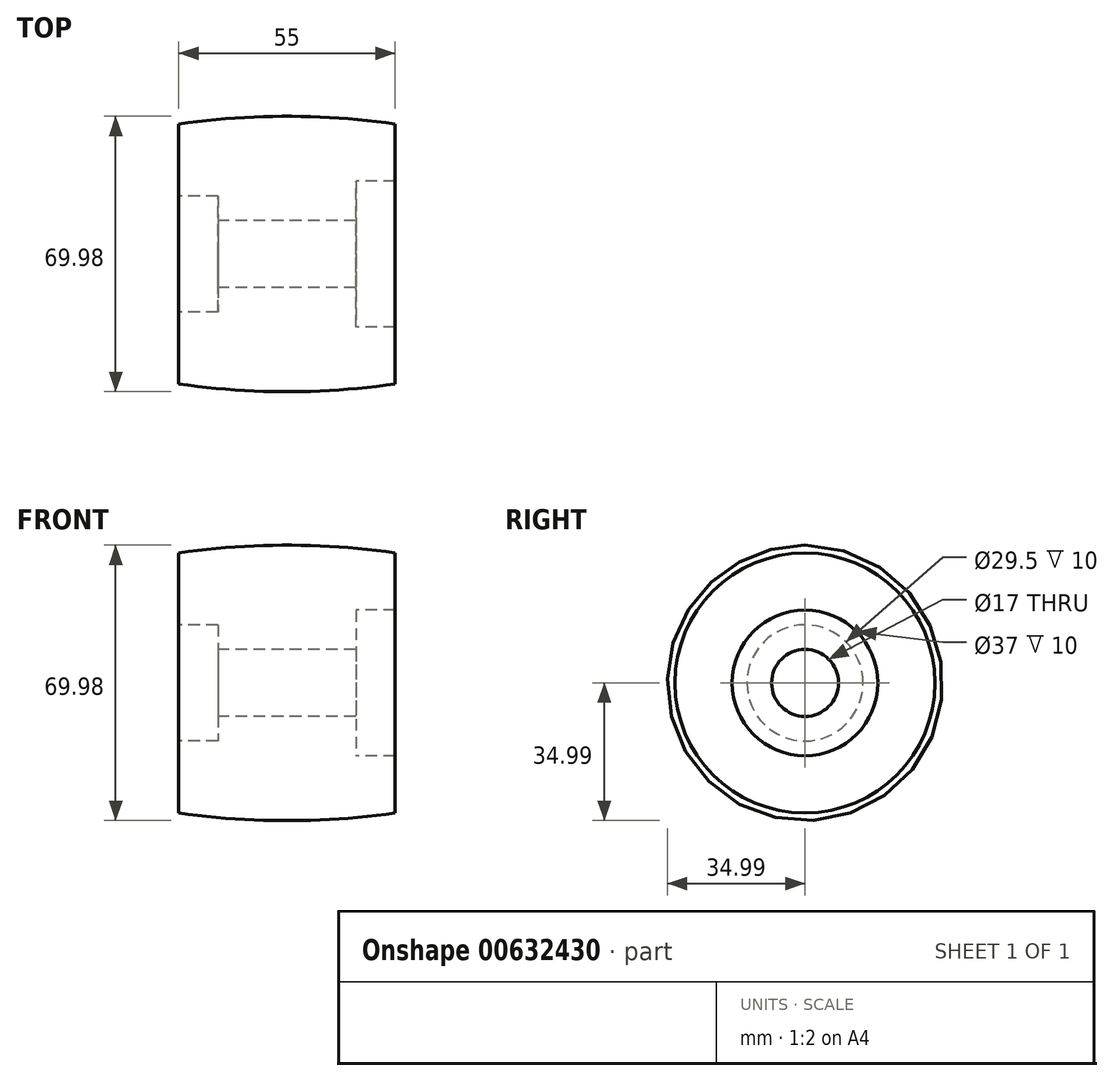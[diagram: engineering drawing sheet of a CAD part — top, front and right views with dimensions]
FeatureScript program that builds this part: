
annotation { "Feature Type Name" : "Feature", "Feature Type Description" : "" }
export const myFeature = defineFeature(function(context is Context, id is Id, definition is map)
    precondition{}
    {
        {
            var Q0;
            Q0=qCreatedBy(makeId("Front.planeOp"),FACE);
            var sketch = newSketch(context, id + "F0", { "sketchPlane" : qUnion([Q0])});
            skLineSegment(sketch, "E0", {"start": v(-27.5, 14.75) * mm, "end": v(-27.5, 33.02) * mm});
            skLineSegment(sketch, "E1", {"start": v(0, 96.82) * mm, "end": v(0, 0) * mm, "construction": true});
            skPoint(sketch, "E2.orphan", {"position": v(0, 0) * mm});
            skLineSegment(sketch, "E3.MirrorCS", {"start": v(27.5, 18.5) * mm, "end": v(27.5, 33.02) * mm});
            skLineSegment(sketch, "E4", {"start": v(-27.5, 0) * mm, "end": v(27.5, 0) * mm, "construction": true});
            skLineSegment(sketch, "E5", {"start": v(-17.5, 8.5) * mm, "end": v(17.5, 8.5) * mm});
            skLineSegment(sketch, "E6", {"start": v(-27.5, 14.75) * mm, "end": v(-17.5, 14.75) * mm});
            skLineSegment(sketch, "E7", {"start": v(-17.5, 14.75) * mm, "end": v(-17.5, 8.5) * mm});
            skPoint(sketch, "E8.orphan", {"position": v(-27.5, 8.5) * mm});
            skLineSegment(sketch, "E9", {"start": v(17.5, 8.5) * mm, "end": v(17.5, 18.5) * mm});
            skLineSegment(sketch, "E10", {"start": v(17.5, 18.5) * mm, "end": v(27.5, 18.5) * mm});
            skLineSegment(sketch, "E11", {"start": v(0, 0) * mm, "end": v(3.3, -349.98) * mm, "construction": true});
            skArc(sketch, "E12", {"start": v(27.5, 33.02) * mm, "mid": v(0, 35) * mm, "end": v(-27.5, 33.02) * mm});
            skSolve(sketch);
        }
        {
            var Q0;
            Q0=makeQuery(id+"F0.imprint","IMPRINT",FACE,{"disambiguationData":[TD([[makeQuery(id+"F0.imprint","IMPRINT",EDGE,{"derivedFrom":sQuery(id+"F0.wireOp",EDGE,"E0")}),-1.0]])]});
            var Q1;
            Q1=sQuery(id+"F0.wireOp",EDGE,"E4");
            revolve(context, id + "F1", {"entities" : qUnion([Q0]), "axis" : qUnion([Q1]), "revolveType" : RevolveType.FULL});
        }
    });
